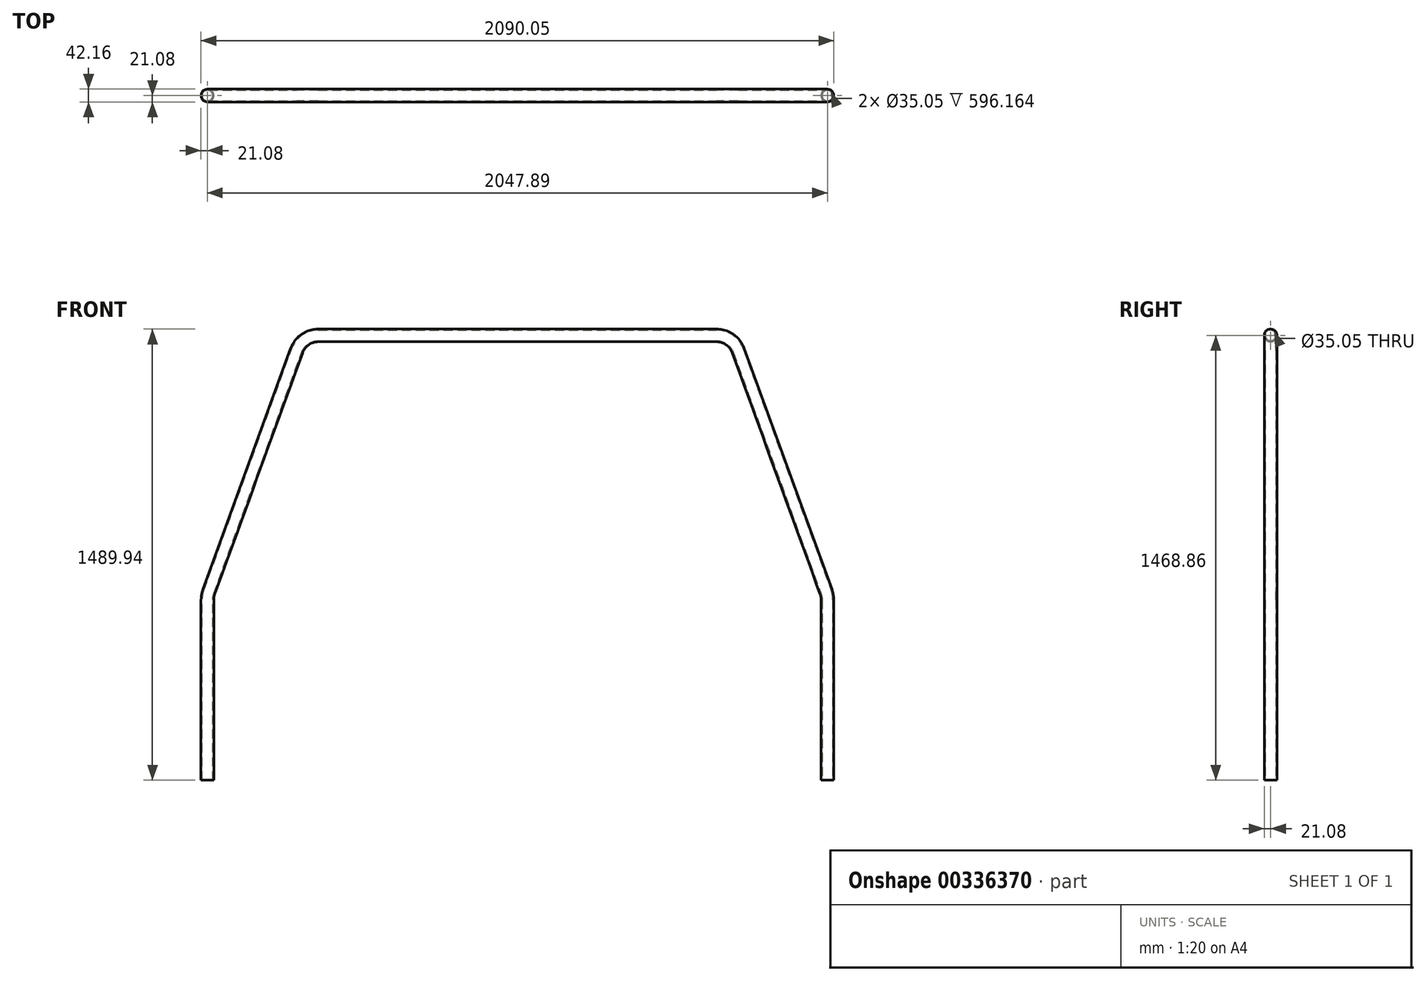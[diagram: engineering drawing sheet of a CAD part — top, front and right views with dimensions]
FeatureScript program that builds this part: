
annotation { "Feature Type Name" : "Feature", "Feature Type Description" : "" }
export const myFeature = defineFeature(function(context is Context, id is Id, definition is map)
    precondition{}
    {
        {
            var Q0;
            Q0=qCreatedBy(makeId("Top.planeOp"),FACE);
            var sketch = newSketch(context, id + "F0", { "sketchPlane" : qUnion([Q0])});
            skCircle(sketch, "E0", {"center": v(0, 0) * mm, "radius": 21.08 * mm});
            skCircle(sketch, "E1", {"center": v(0, 0) * mm, "radius": 17.53 * mm});
            skSolve(sketch);
        }
        {
            var Q0;
            Q0=qCreatedBy(makeId("Front.planeOp"),FACE);
            var sketch = newSketch(context, id + "F1", { "sketchPlane" : qUnion([Q0])});
            skLineSegment(sketch, "E2", {"start": v(0, 0) * mm, "end": v(0, 596.16) * mm});
            skLineSegment(sketch, "E3", {"start": v(4.6, 622.23) * mm, "end": v(294.5, 1418.72) * mm});
            skLineSegment(sketch, "E4", {"start": v(366.1, 1468.85) * mm, "end": v(1681.79, 1468.85) * mm});
            skLineSegment(sketch, "E5", {"start": v(1753.4, 1418.72) * mm, "end": v(2043.3, 622.23) * mm});
            skLineSegment(sketch, "E6", {"start": v(2047.89, 596.16) * mm, "end": v(2047.89, 0) * mm});
            skPoint(sketch, "E7.visualSharp", {"position": v(0, 609.6) * mm});
            skArc(sketch, "E7.filletArc", {"start": v(4.6, 622.23) * mm, "mid": v(1.16, 609.4) * mm, "end": v(0, 596.16) * mm});
            skPoint(sketch, "E8.visualSharp", {"position": v(312.74, 1468.85) * mm});
            skArc(sketch, "E8.filletArc", {"start": v(366.1, 1468.85) * mm, "mid": v(322.4, 1455.07) * mm, "end": v(294.5, 1418.72) * mm});
            skPoint(sketch, "E9.visualSharp", {"position": v(1735.14, 1468.85) * mm});
            skArc(sketch, "E9.filletArc", {"start": v(1753.4, 1418.72) * mm, "mid": v(1725.5, 1455.07) * mm, "end": v(1681.79, 1468.85) * mm});
            skPoint(sketch, "E10.visualSharp", {"position": v(2047.89, 609.6) * mm});
            skArc(sketch, "E10.filletArc", {"start": v(2047.89, 596.16) * mm, "mid": v(2046.73, 609.4) * mm, "end": v(2043.3, 622.23) * mm});
            skSolve(sketch);
        }
        {
            var Q0;
            Q0 = qSketchRegion(id + "F0", true);
            var Q1;
            Q1 = qConstructionFilter(qBodyType(qCreatedBy(id + "F1" ,EDGE), BodyType.WIRE), ConstructionObject.NO);
            sweep(context, id + "F2", {"profiles" : qUnion([Q0]), "path" : qUnion([Q1])});
        }
    });
